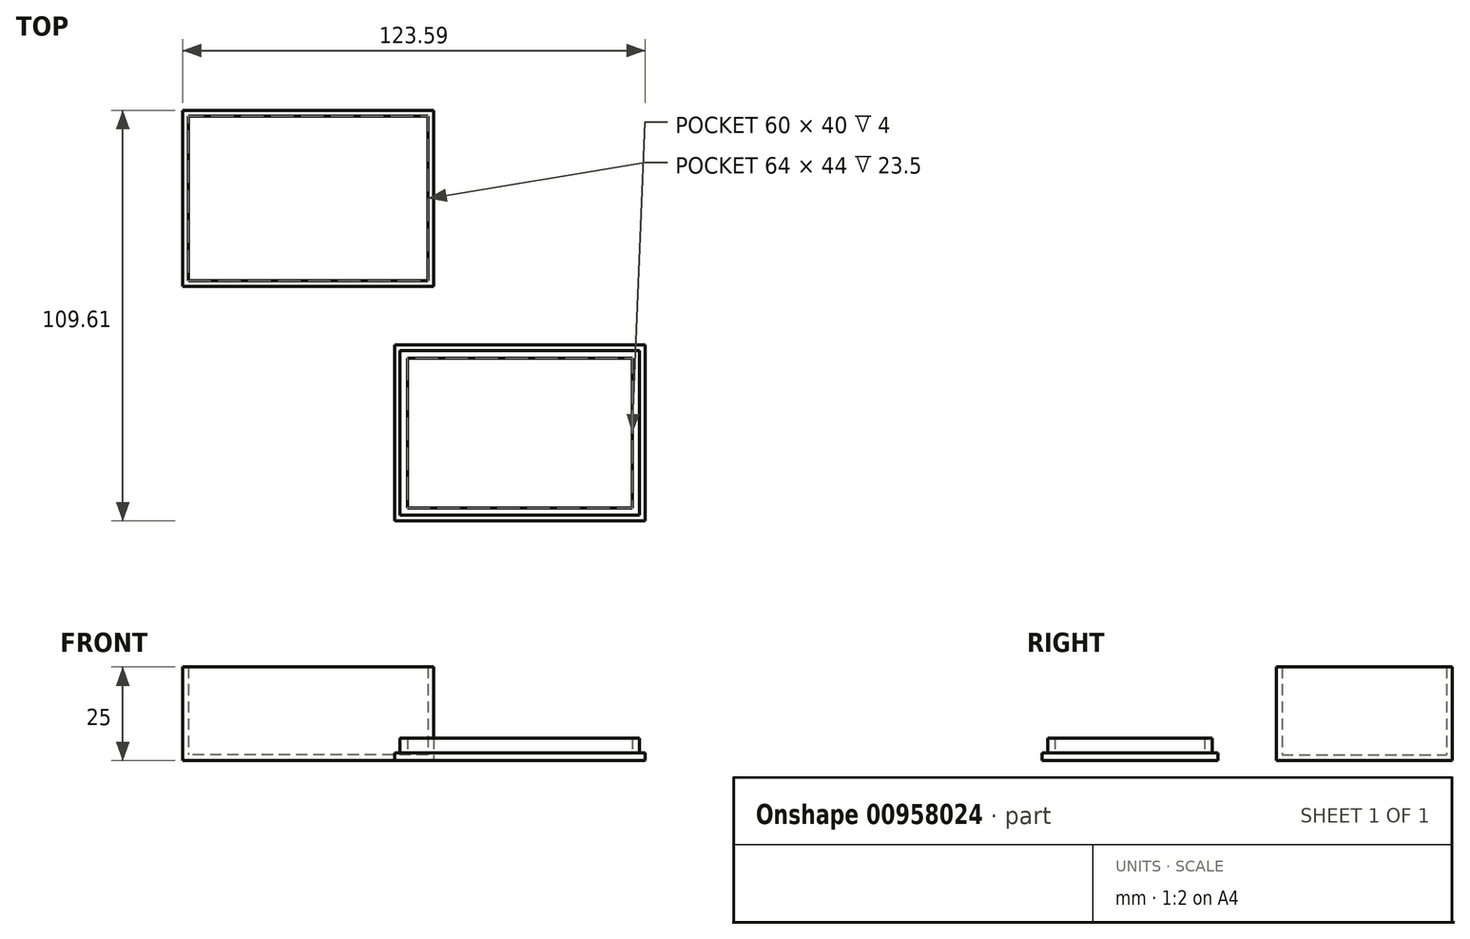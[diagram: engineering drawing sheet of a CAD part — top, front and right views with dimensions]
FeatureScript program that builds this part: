
annotation { "Feature Type Name" : "Feature", "Feature Type Description" : "" }
export const myFeature = defineFeature(function(context is Context, id is Id, definition is map)
    precondition{}
    {
        {
            var Q0;
            Q0=qCreatedBy(makeId("Top.planeOp"),FACE);
            var sketch = newSketch(context, id + "F0", { "sketchPlane" : qUnion([Q0])});
            skLineSegment(sketch, "E0.bottom", {"start": v(9.56, -1.12) * mm, "end": v(-57.44, -1.12) * mm});
            skLineSegment(sketch, "E0.top", {"start": v(9.56, 45.88) * mm, "end": v(-57.44, 45.88) * mm});
            skLineSegment(sketch, "E0.left", {"start": v(9.56, -1.12) * mm, "end": v(9.56, 45.88) * mm});
            skLineSegment(sketch, "E0.right", {"start": v(-57.44, -1.12) * mm, "end": v(-57.44, 45.88) * mm});
            skPoint(sketch, "E0.middle", {"position": v(-23.94, 22.38) * mm});
            skSolve(sketch);
        }
        {
            var Q0;
            Q0=qSketchRegion(id+"F0",true);
            extrude(context, id + "F1", {"entities" : qUnion([Q0]), "depth" : 25 * mm, "offsetDistance" : 25 * mm});
        }
        {
            var Q0;
            Q0=makeQuery(id+"F1.opExtrude","CAP_FACE",FACE,{"disambiguationData":[OSD([sQuery(id+"F0.wireOp",EDGE,"E0.bottom"),sQuery(id+"F0.wireOp",EDGE,"E0.top"),sQuery(id+"F0.wireOp",EDGE,"E0.left"),sQuery(id+"F0.wireOp",EDGE,"E0.right")])],"isStart":false});
            shell(context, id + "F2", {"entities" : qUnion([Q0]), "thickness" : 1.5 * mm});
        }
        {
            var Q0;
            Q0=qCreatedBy(makeId("Top.planeOp"),FACE);
            var sketch = newSketch(context, id + "F3", { "sketchPlane" : qUnion([Q0])});
            skLineSegment(sketch, "E1.bottom", {"start": v(2.65, -60.23) * mm, "end": v(62.65, -60.23) * mm});
            skLineSegment(sketch, "E1.top", {"start": v(2.65, -20.23) * mm, "end": v(62.65, -20.23) * mm});
            skLineSegment(sketch, "E1.left", {"start": v(2.65, -60.23) * mm, "end": v(2.65, -20.23) * mm});
            skLineSegment(sketch, "E1.right", {"start": v(62.65, -60.23) * mm, "end": v(62.65, -20.23) * mm});
            skPoint(sketch, "E1.middle", {"position": v(32.65, -40.23) * mm});
            skLineSegment(sketch, "E2.bottom", {"start": v(0.65, -18.23) * mm, "end": v(64.65, -18.23) * mm});
            skLineSegment(sketch, "E2.top", {"start": v(0.65, -62.23) * mm, "end": v(64.65, -62.23) * mm});
            skLineSegment(sketch, "E2.left", {"start": v(0.65, -18.23) * mm, "end": v(0.65, -62.23) * mm});
            skLineSegment(sketch, "E2.right", {"start": v(64.65, -18.23) * mm, "end": v(64.65, -62.23) * mm});
            skLineSegment(sketch, "E3.bottom", {"start": v(-0.85, -16.73) * mm, "end": v(66.15, -16.73) * mm});
            skLineSegment(sketch, "E3.top", {"start": v(-0.85, -63.73) * mm, "end": v(66.15, -63.73) * mm});
            skLineSegment(sketch, "E3.left", {"start": v(-0.85, -16.73) * mm, "end": v(-0.85, -63.73) * mm});
            skLineSegment(sketch, "E3.right", {"start": v(66.15, -16.73) * mm, "end": v(66.15, -63.73) * mm});
            skSolve(sketch);
        }
        {
            var Q0;
            Q0=makeQuery(id+"F3.imprint","IMPRINT",FACE,{"disambiguationData":[TD([[makeQuery(id+"F3.imprint","IMPRINT",EDGE,{"derivedFrom":sQuery(id+"F3.wireOp",EDGE,"E2.bottom")}),-1.0]])]});
            extrude(context, id + "F4", {"entities" : qUnion([Q0]), "depth" : 4 * mm, "offsetDistance" : 25 * mm});
        }
        {
            var Q0;
            Q0=makeQuery(id+"F3.imprint","IMPRINT",FACE,{"disambiguationData":[TD([[makeQuery(id+"F3.imprint","IMPRINT",EDGE,{"derivedFrom":sQuery(id+"F3.wireOp",EDGE,"E1.bottom")}),1.0]])]});
            var Q1;
            Q1=makeQuery(id+"F3.imprint","IMPRINT",FACE,{"disambiguationData":[TD([[makeQuery(id+"F3.imprint","IMPRINT",EDGE,{"derivedFrom":sQuery(id+"F3.wireOp",EDGE,"E2.bottom")}),-1.0]])]});
            var Q2;
            Q2=makeQuery(id+"F3.imprint","IMPRINT",FACE,{"disambiguationData":[TD([[makeQuery(id+"F3.imprint","IMPRINT",EDGE,{"derivedFrom":sQuery(id+"F3.wireOp",EDGE,"E3.bottom")}),-1.0]])]});
            var Q3;
            Q3=makeQuery(id+"F4.opExtrude","CAP_FACE",FACE,{"disambiguationData":[OSD([sQuery(id+"F3.wireOp",EDGE,"E2.bottom"),sQuery(id+"F3.wireOp",EDGE,"E2.top"),sQuery(id+"F3.wireOp",EDGE,"E2.left"),sQuery(id+"F3.wireOp",EDGE,"E2.right"),sQuery(id+"F3.wireOp",EDGE,"E3.bottom"),sQuery(id+"F3.wireOp",EDGE,"E3.top"),sQuery(id+"F3.wireOp",EDGE,"E3.left"),sQuery(id+"F3.wireOp",EDGE,"E3.right")])],"isStart":false});
            extrude(context, id + "F5", {"entities" : qUnion([Q0, Q1, Q2, Q3]), "operationType" : NewBodyOperationType.ADD, "depth" : 2 * mm, "offsetDistance" : 25 * mm});
        }
    });
